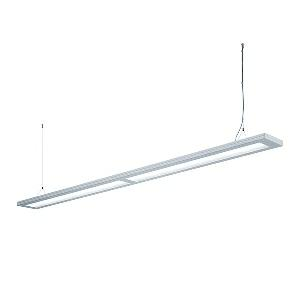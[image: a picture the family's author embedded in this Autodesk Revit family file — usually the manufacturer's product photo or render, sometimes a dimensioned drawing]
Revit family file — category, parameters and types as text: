
# Revit family: lavigo_-_dpp_960_d_vtl_00682565_ae96
name_source: partatom
category: Lighting Fixtures
units: mm (PartAtom-declared; Revit-internal decimal feet)

## family parameters
Cut with Voids When Loaded = No
Host = Face
Light Source = No
Part Type = Normal
Room Calculation Point = No
Round Connector Dimension = Use Diameter
Shared = No

## types (1)
- LAVIGO - DPP 960/D VTL (1 x LED VTL, 7500 lm, 3000-6500K)
    Apparent Load = 57 VA
    Approval mark = CE
    CIE Flux Codes = 65 90 97 29 100
    Color Rendering = 80-89
    Color Temperature = 3000-6500K
    Control Gear = Electronic ballast
    Default Elevation = 1800 mm
    Description = DPP 960/D|Suspended luminaire|light source: LED  3000-6500 K  Energy efficiency category A/A+/A++|   4000 K 4000 K Energy efficiency category A++|connected load: 220-240 V, 50/60 Hz|Power consumption: approx. 57 W|standby: approx. 0,98|luminous flux: 7500 lm|luminous efficacy: 131 lm/W|light distribution: Direct/indirect|direct ratio: approx. 29 %|color rendering index (CRI): >= 80|chromaticity tolerance:  3 SDCM|System of protection: IP 20|technology: Continuously dimmable|luminaire body|material: Steel/plastic|surface: Painted|colour: Silver metallic|lamp cover: Polycarbonate (PC), Clear|mains lead: 1.00 m With free stranded wires|Fastening: Steel cable 0.3 - 0.7 m|decorative contrast side parts: Flint grey|glare control: Prism aperture|luminance(L65): <= 1500 cd/m|unified glare rating(4H 8H): <=  16|special features: DALI - dimming via digital rotary dimmer, DALI Load 2x, Integration into DALI light management system for biodynamic light VTL, Light forming, Separated, direct and indirect light individually adjustable|
    Frequency = 50 Hz
    Height = 36 mm  [stored 0.11811 ft]
    Lamp = 1 x LED VTL
    Lamp Light Flux = 7500 lm
    Lamp count = 1
    Length = 2430 mm
    Luminous efficacy = 132 lm/W
    Manufacturer = Waldmann
    ModVariant = No
    Model = 00682565
    Mounting Place = Ceiling
    Mounting Type = Pendant
    Number of Poles = 1
    OnlyDefault = Yes
    Power Factor = 1
    Product Name = LAVIGO - DPP 960/D VTL
    Product group = Suspended luminaire
    ProductGroupID = 9
    Protection Class = Protection class I
    Protection Degree = IP 20
    RLX_Detail_Level = 1
    RLX_Emergency_Light_Flux = 0 lm
    RLX_Emergency_Type = 0
    RLX_Emergency_Type_DB = No
    RlxData = <blob elided: 25781 chars, md5=b8e70ab2>
    Socket = socket
    Standby Power = 0 W
    System Light Flux = 7500 lm
    System Power = 57 W
    Type Comments = Product without accessories
    Type Image = 121742000-00681441.jpg
    URL = http://relux.com
    VarID = ---
    Voltage = 230 V
    Voltage Range = 220-240 V
    Weight = 0.00 kg
    Width = 200 mm

note: [stored X ft] marks values corroborated as IEEE doubles in the binary element streams (Revit-internal decimal feet)

## geometry (parser evidence)
native form markers: Blend x4, Sweep x13
no freeform markers — native parametric forms only
